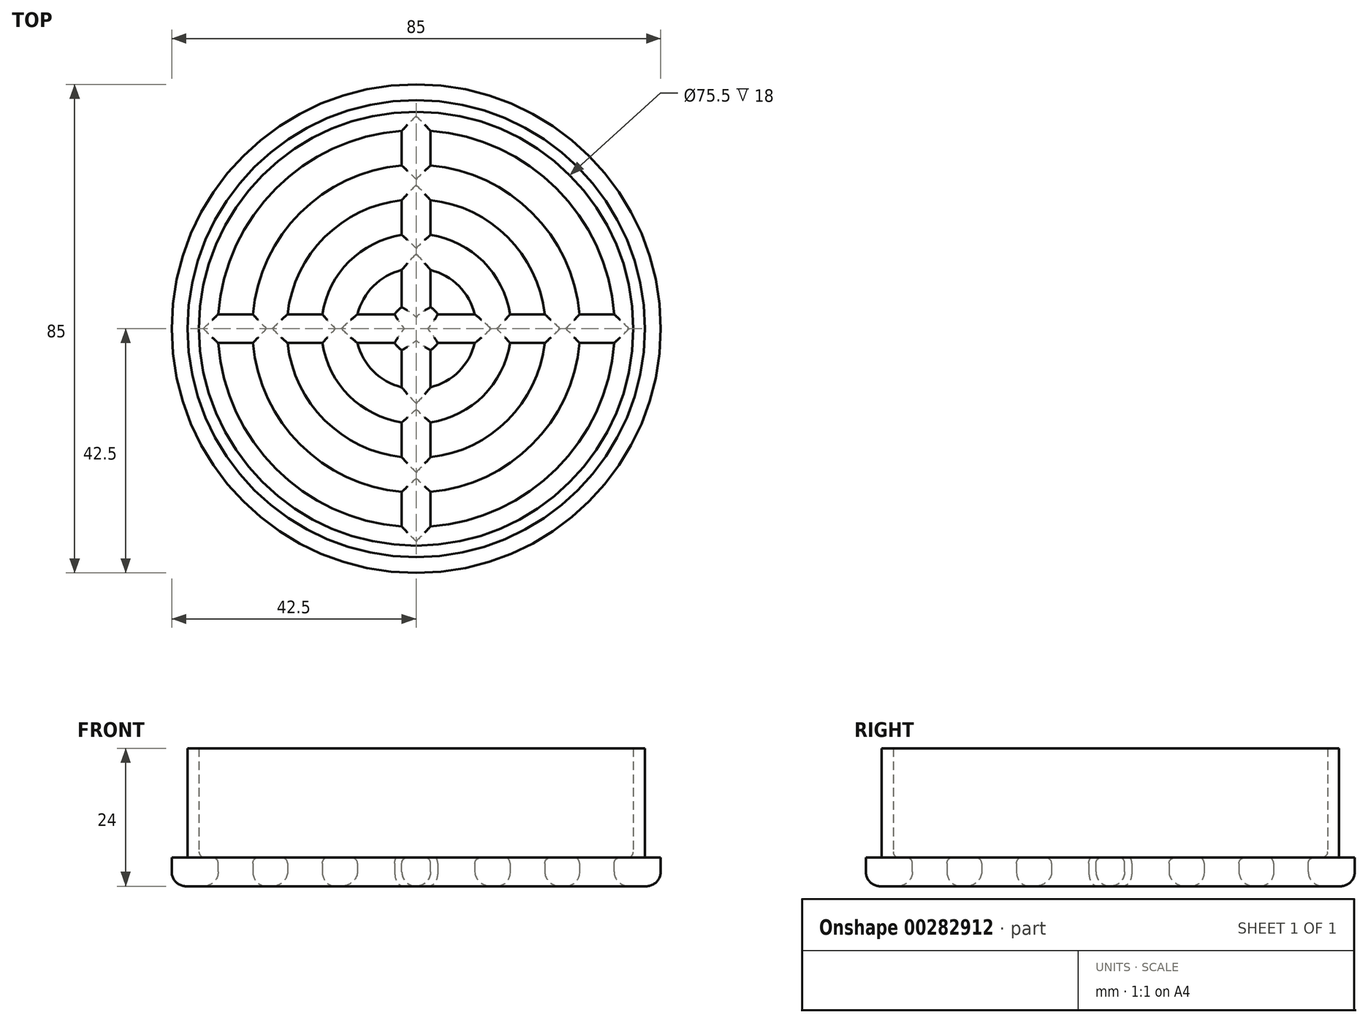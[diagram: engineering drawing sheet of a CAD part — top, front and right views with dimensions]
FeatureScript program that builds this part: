
annotation { "Feature Type Name" : "Feature", "Feature Type Description" : "" }
export const myFeature = defineFeature(function(context is Context, id is Id, definition is map)
    precondition{}
    {
        {
            var Q0;
            Q0=qCreatedBy(makeId("Top.planeOp"),FACE);
            var sketch = newSketch(context, id + "F0", { "sketchPlane" : qUnion([Q0])});
            skCircle(sketch, "E0", {"center": v(0, 0) * mm, "radius": 42.5 * mm});
            skCircle(sketch, "E1", {"center": v(0, 0) * mm, "radius": 34.5 * mm});
            skCircle(sketch, "E2", {"center": v(0, 0) * mm, "radius": 28.5 * mm});
            skCircle(sketch, "E3", {"center": v(0, 0) * mm, "radius": 22.5 * mm});
            skCircle(sketch, "E4", {"center": v(0, 0) * mm, "radius": 16.5 * mm});
            skCircle(sketch, "E5", {"center": v(0, 0) * mm, "radius": 10.5 * mm});
            skCircle(sketch, "E6", {"center": v(0, 0) * mm, "radius": 4.5 * mm});
            skSolve(sketch);
        }
        {
            var Q0;
            Q0 = qSketchRegion(id + "F0", true);
            var Q1;
            Q1=makeQuery(id+"F0.imprint","IMPRINT",FACE,{"disambiguationData":[TD([[makeQuery(id+"F0.imprint","IMPRINT",EDGE,{"derivedFrom":sQuery(id+"F0.wireOp",EDGE,"E2")}),1.0]])]});
            var Q2;
            Q2=makeQuery(id+"F0.imprint","IMPRINT",FACE,{"disambiguationData":[TD([[makeQuery(id+"F0.imprint","IMPRINT",EDGE,{"derivedFrom":sQuery(id+"F0.wireOp",EDGE,"E4")}),1.0]])]});
            var Q3;
            Q3=makeQuery(id+"F0.imprint","IMPRINT",FACE,{"disambiguationData":[TD([[makeQuery(id+"F0.imprint","IMPRINT",EDGE,{"derivedFrom":sQuery(id+"F0.wireOp",EDGE,"E6")}),1.0]])]});
            extrude(context, id + "F1", {"entities" : qUnion([Q0, Q1, Q2, Q3]), "depth" : 5 * mm});
        }
        {
            var Q0;
            Q0=makeQuery(id+"F1.opExtrude","CAP_FACE",FACE,{"disambiguationData":[OSD([sQuery(id+"F0.wireOp",EDGE,"E0"),sQuery(id+"F0.wireOp",EDGE,"E1")])],"isStart":false});
            var sketch = newSketch(context, id + "F2", { "sketchPlane" : qUnion([Q0])});
            skSolve(sketch);
        }
        {
            var Q0;
            Q0=makeQuery(id+"F1.opExtrude","CAP_FACE",FACE,{"disambiguationData":[OSD([sQuery(id+"F0.wireOp",EDGE,"E0"),sQuery(id+"F0.wireOp",EDGE,"E1")])],"isStart":false});
            var sketch = newSketch(context, id + "F3", { "sketchPlane" : qUnion([Q0])});
            skLineSegment(sketch, "E7", {"start": v(0, 0) * mm, "end": v(42.5, 0) * mm});
            skLineSegment(sketch, "E8", {"start": v(0, 0) * mm, "end": v(-42.5, 0) * mm});
            skLineSegment(sketch, "E9", {"start": v(0, 0) * mm, "end": v(0, 42.5) * mm});
            skLineSegment(sketch, "E10", {"start": v(0, 0) * mm, "end": v(0, -42.5) * mm});
            skArc(sketch, "E11.0.startCap", {"start": v(0, 2.5) * mm, "mid": v(2.5, 0) * mm, "end": v(0, -2.5) * mm});
            skArc(sketch, "E11.0.endCap", {"start": v(-42.5, -2.5) * mm, "mid": v(-45, 0) * mm, "end": v(-42.5, 2.5) * mm});
            skLineSegment(sketch, "E11.0.left", {"start": v(0, -2.5) * mm, "end": v(-42.5, -2.5) * mm});
            skLineSegment(sketch, "E11.0.right", {"start": v(0, 2.5) * mm, "end": v(-42.5, 2.5) * mm});
            skArc(sketch, "E11.1.startCap", {"start": v(2.5, 0) * mm, "mid": v(0, -2.5) * mm, "end": v(-2.5, 0) * mm});
            skArc(sketch, "E11.1.endCap", {"start": v(-2.5, 42.5) * mm, "mid": v(0, 45) * mm, "end": v(2.5, 42.5) * mm});
            skLineSegment(sketch, "E11.1.left", {"start": v(-2.5, 0) * mm, "end": v(-2.5, 42.5) * mm});
            skLineSegment(sketch, "E11.1.right", {"start": v(2.5, 0) * mm, "end": v(2.5, 42.5) * mm});
            skArc(sketch, "E11.2.startCap", {"start": v(0, -2.5) * mm, "mid": v(-2.5, 0) * mm, "end": v(0, 2.5) * mm});
            skArc(sketch, "E11.2.endCap", {"start": v(42.5, 2.5) * mm, "mid": v(45, 0) * mm, "end": v(42.5, -2.5) * mm});
            skLineSegment(sketch, "E11.2.left", {"start": v(0, 2.5) * mm, "end": v(42.5, 2.5) * mm});
            skLineSegment(sketch, "E11.2.right", {"start": v(0, -2.5) * mm, "end": v(42.5, -2.5) * mm});
            skArc(sketch, "E11.3.startCap", {"start": v(-2.5, 0) * mm, "mid": v(0, 2.5) * mm, "end": v(2.5, 0) * mm});
            skArc(sketch, "E11.3.endCap", {"start": v(2.5, -42.5) * mm, "mid": v(0, -45) * mm, "end": v(-2.5, -42.5) * mm});
            skLineSegment(sketch, "E11.3.left", {"start": v(2.5, 0) * mm, "end": v(2.5, -42.5) * mm});
            skLineSegment(sketch, "E11.3.right", {"start": v(-2.5, 0) * mm, "end": v(-2.5, -42.5) * mm});
            skSolve(sketch);
        }
        {
            var Q0;
            {var subQ0=sQuery(id+"F3.wireOp",EDGE,"E11.1.left");var subQ5=sQuery(id+"F3.wireOp",EDGE,"E11.0.right");var subQ6=makeQuery(id+"F3.imprint","INTERSECT",VERTEX,{"derivedFrom":[subQ5,subQ0]});Q0=makeQuery(id+"F3.imprint","IMPRINT",FACE,{"disambiguationData":[TD([[makeQuery(id+"F3.imprint","IMPRINT",EDGE,{"disambiguationData":[TD([[subQ6,-1.0]])],"derivedFrom":subQ5}),1.0]])]});}
            var Q1;
            {var subQ0=sQuery(id+"F3.wireOp",EDGE,"E11.3.right");var subQ5=sQuery(id+"F3.wireOp",EDGE,"E11.0.left");var subQ6=makeQuery(id+"F3.imprint","INTERSECT",VERTEX,{"derivedFrom":[subQ5,subQ0]});Q1=makeQuery(id+"F3.imprint","IMPRINT",FACE,{"disambiguationData":[TD([[makeQuery(id+"F3.imprint","IMPRINT",EDGE,{"disambiguationData":[TD([[subQ6,-1.0]])],"derivedFrom":subQ5}),-1.0]])]});}
            var Q2;
            {var subQ0=sQuery(id+"F3.wireOp",EDGE,"E11.0.right");var subQ5=sQuery(id+"F3.wireOp",EDGE,"E11.1.left");var subQ6=makeQuery(id+"F3.imprint","INTERSECT",VERTEX,{"derivedFrom":[subQ0,subQ5]});Q2=makeQuery(id+"F3.imprint","IMPRINT",FACE,{"disambiguationData":[TD([[makeQuery(id+"F3.imprint","IMPRINT",EDGE,{"disambiguationData":[TD([[subQ6,-1.0]])],"derivedFrom":subQ5}),-1.0]])]});}
            var Q3;
            {var subQ0=sQuery(id+"F3.wireOp",EDGE,"E11.2.left");var subQ5=sQuery(id+"F3.wireOp",EDGE,"E11.1.right");var subQ6=makeQuery(id+"F3.imprint","INTERSECT",VERTEX,{"derivedFrom":[subQ5,subQ0]});Q3=makeQuery(id+"F3.imprint","IMPRINT",FACE,{"disambiguationData":[TD([[makeQuery(id+"F3.imprint","IMPRINT",EDGE,{"disambiguationData":[TD([[subQ6,-1.0]])],"derivedFrom":subQ5}),1.0]])]});}
            var Q4;
            {var subQ0=sQuery(id+"F3.wireOp",EDGE,"E11.1.right");var subQ5=sQuery(id+"F3.wireOp",EDGE,"E11.2.left");var subQ6=makeQuery(id+"F3.imprint","INTERSECT",VERTEX,{"derivedFrom":[subQ0,subQ5]});Q4=makeQuery(id+"F3.imprint","IMPRINT",FACE,{"disambiguationData":[TD([[makeQuery(id+"F3.imprint","IMPRINT",EDGE,{"disambiguationData":[TD([[subQ6,-1.0]])],"derivedFrom":subQ5}),-1.0]])]});}
            var Q5;
            {var subQ0=sQuery(id+"F3.wireOp",EDGE,"E11.3.left");var subQ5=sQuery(id+"F3.wireOp",EDGE,"E11.2.right");var subQ6=makeQuery(id+"F3.imprint","INTERSECT",VERTEX,{"derivedFrom":[subQ5,subQ0]});Q5=makeQuery(id+"F3.imprint","IMPRINT",FACE,{"disambiguationData":[TD([[makeQuery(id+"F3.imprint","IMPRINT",EDGE,{"disambiguationData":[TD([[subQ6,-1.0]])],"derivedFrom":subQ5}),1.0]])]});}
            var Q6;
            {var subQ0=sQuery(id+"F3.wireOp",EDGE,"E11.2.right");var subQ5=sQuery(id+"F3.wireOp",EDGE,"E11.3.left");var subQ6=makeQuery(id+"F3.imprint","INTERSECT",VERTEX,{"derivedFrom":[subQ0,subQ5]});Q6=makeQuery(id+"F3.imprint","IMPRINT",FACE,{"disambiguationData":[TD([[makeQuery(id+"F3.imprint","IMPRINT",EDGE,{"disambiguationData":[TD([[subQ6,-1.0]])],"derivedFrom":subQ5}),-1.0]])]});}
            var Q7;
            {var subQ0=sQuery(id+"F3.wireOp",EDGE,"E11.0.left");var subQ5=sQuery(id+"F3.wireOp",EDGE,"E11.3.right");var subQ6=makeQuery(id+"F3.imprint","INTERSECT",VERTEX,{"derivedFrom":[subQ0,subQ5]});Q7=makeQuery(id+"F3.imprint","IMPRINT",FACE,{"disambiguationData":[TD([[makeQuery(id+"F3.imprint","IMPRINT",EDGE,{"disambiguationData":[TD([[subQ6,-1.0]])],"derivedFrom":subQ5}),1.0]])]});}
            extrude(context, id + "F4", {"entities" : qUnion([Q0, Q1, Q2, Q3, Q4, Q5, Q6, Q7]), "operationType" : NewBodyOperationType.ADD, "oppositeDirection" : true, "depth" : 5 * mm});
        }
        {
            var Q0;
            Q0=makeQuery(id+"F2.imprint","IMPRINT",FACE,{"disambiguationData":[TD([[makeQuery(id+"F2.imprint","IMPRINT",EDGE,{"derivedFrom":makeQuery(id+"F1.opExtrude","CAP_EDGE",EDGE,{"disambiguationData":[OSD([sQuery(id+"F0.wireOp",EDGE,"E0")])],"isStart":false})}),1.0]])]});
            var sketch = newSketch(context, id + "F5", { "sketchPlane" : qUnion([Q0])});
            skCircle(sketch, "E12", {"center": v(0, 0) * mm, "radius": 39.75 * mm});
            skCircle(sketch, "E13", {"center": v(0, 0) * mm, "radius": 37.75 * mm});
            skSolve(sketch);
        }
        {
            var Q0;
            Q0=makeQuery(id+"F5.imprint","IMPRINT",FACE,{"disambiguationData":[TD([[makeQuery(id+"F5.imprint","IMPRINT",EDGE,{"derivedFrom":sQuery(id+"F5.wireOp",EDGE,"E12")}),1.0]])]});
            extrude(context, id + "F6", {"entities" : qUnion([Q0]), "operationType" : NewBodyOperationType.ADD, "depth" : 19 * mm});
        }
        {
            var Q0;
            {var subQ0=sQuery(id+"F3.wireOp",EDGE,"E11.3.left");var subQ1=sQuery(id+"F3.wireOp",EDGE,"E11.2.right");var subQ2=sQuery(id+"F3.wireOp",EDGE,"E11.2.left");var subQ3=sQuery(id+"F3.wireOp",EDGE,"E11.1.right");var subQ4=sQuery(id+"F0.wireOp",EDGE,"E1");var subQ5=sQuery(id+"F3.wireOp",EDGE,"E11.1.left");var subQ6=sQuery(id+"F3.wireOp",EDGE,"E11.0.right");var subQ7=sQuery(id+"F3.wireOp",EDGE,"E11.3.right");var subQ8=sQuery(id+"F3.wireOp",EDGE,"E11.0.left");Q0=makeQuery(id+"F4.boolean.opBoolean","MERGE",FACE,{"derivedFrom":[makeQuery(id+"F1.opExtrude","CAP_FACE",FACE,{"disambiguationData":[OSD([sQuery(id+"F0.wireOp",EDGE,"E0"),subQ4])],"isStart":true}),makeQuery(id+"F1.opExtrude","CAP_FACE",FACE,{"disambiguationData":[OSD([sQuery(id+"F0.wireOp",EDGE,"E2"),sQuery(id+"F0.wireOp",EDGE,"E3")])],"isStart":true}),makeQuery(id+"F1.opExtrude","CAP_FACE",FACE,{"disambiguationData":[OSD([sQuery(id+"F0.wireOp",EDGE,"E4"),sQuery(id+"F0.wireOp",EDGE,"E5")])],"isStart":true}),makeQuery(id+"F1.opExtrude","CAP_FACE",FACE,{"disambiguationData":[OSD([sQuery(id+"F0.wireOp",EDGE,"E6")])],"isStart":true}),makeQuery(id+"F4.opExtrude","CAP_FACE",FACE,{"disambiguationData":[OSD([subQ4,subQ8,subQ1,subQ0,subQ7])],"isStart":false}),makeQuery(id+"F4.opExtrude","CAP_FACE",FACE,{"disambiguationData":[OSD([subQ4,subQ8,subQ6,subQ5,subQ7])],"isStart":false}),makeQuery(id+"F4.opExtrude","CAP_FACE",FACE,{"disambiguationData":[OSD([subQ4,subQ6,subQ5,subQ3,subQ2])],"isStart":false}),makeQuery(id+"F4.opExtrude","CAP_FACE",FACE,{"disambiguationData":[OSD([subQ4,subQ3,subQ2,subQ1,subQ0])],"isStart":false})]});}
            fillet(context, id + "F7", {"entities" : qUnion([Q0]), "radius" : 2.5 * mm, "tangentPropagation" : true, "allowEdgeOverflow" : false});
        }
        {
            var Q0;
            {var subQ0=sQuery(id+"F3.wireOp",EDGE,"E11.1.right");var subQ1=sQuery(id+"F3.wireOp",EDGE,"E11.1.left");var subQ2=sQuery(id+"F3.wireOp",EDGE,"E11.0.left");var subQ3=sQuery(id+"F0.wireOp",EDGE,"E6");var subQ4=sQuery(id+"F0.wireOp",EDGE,"E5");var subQ5=sQuery(id+"F0.wireOp",EDGE,"E1");var subQ6=sQuery(id+"F0.wireOp",EDGE,"E4");var subQ7=sQuery(id+"F3.wireOp",EDGE,"E11.0.right");var subQ8=sQuery(id+"F0.wireOp",EDGE,"E2");var subQ9=sQuery(id+"F0.wireOp",EDGE,"E3");var subQ10=sQuery(id+"F3.wireOp",EDGE,"E11.2.left");var subQ11=sQuery(id+"F3.wireOp",EDGE,"E11.2.right");var subQ12=sQuery(id+"F3.wireOp",EDGE,"E11.3.left");var subQ13=sQuery(id+"F3.wireOp",EDGE,"E11.3.right");Q0=makeQuery(id+"F6.boolean.opBoolean","SPLIT",FACE,{"disambiguationData":[TD([makeQuery(id+"F1.opExtrude","SWEPT_FACE",FACE,{"disambiguationData":[OSD([subQ5])]})])],"derivedFrom":makeQuery(id+"F4.boolean.opBoolean","MERGE",FACE,{"derivedFrom":[makeQuery(id+"F1.opExtrude","CAP_FACE",FACE,{"disambiguationData":[OSD([sQuery(id+"F0.wireOp",EDGE,"E0"),subQ5])],"isStart":false}),makeQuery(id+"F1.opExtrude","CAP_FACE",FACE,{"disambiguationData":[OSD([subQ8,subQ9])],"isStart":false}),makeQuery(id+"F1.opExtrude","CAP_FACE",FACE,{"disambiguationData":[OSD([subQ6,subQ4])],"isStart":false}),makeQuery(id+"F1.opExtrude","CAP_FACE",FACE,{"disambiguationData":[OSD([subQ3])],"isStart":false}),makeQuery(id+"F4.opExtrude","CAP_FACE",FACE,{"disambiguationData":[OSD([subQ5,subQ2,subQ11,subQ12,subQ13])],"isStart":true}),makeQuery(id+"F4.opExtrude","CAP_FACE",FACE,{"disambiguationData":[OSD([subQ5,subQ2,subQ7,subQ1,subQ13])],"isStart":true}),makeQuery(id+"F4.opExtrude","CAP_FACE",FACE,{"disambiguationData":[OSD([subQ5,subQ7,subQ1,subQ0,subQ10])],"isStart":true}),makeQuery(id+"F4.opExtrude","CAP_FACE",FACE,{"disambiguationData":[OSD([subQ5,subQ0,subQ10,subQ11,subQ12])],"isStart":true})]})});}
            fillet(context, id + "F8", {"entities" : qUnion([Q0]), "radius" : 1 * mm, "tangentPropagation" : true, "allowEdgeOverflow" : false});
        }
    });
